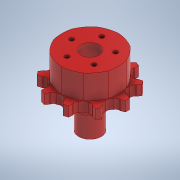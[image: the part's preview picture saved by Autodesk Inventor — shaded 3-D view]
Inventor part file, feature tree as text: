
AUTODESK INVENTOR PART (.ipt)
format: ipt  version: 2020 (Build 240168000, 168)  size: 395,264 bytes
history: native  units: mm
features: other x4, extrude x2, sketch x2
ambient origin geometry x8: Origin, YZ Plane, XZ Plane, XY Plane, X Axis, Y Axis, Z Axis, Center Point
bodies: Body1 (feature_tree)
feature tree (8):
  other  "Cilindric_rotate.ipt"
  extrude  "Выдавливание1"  Depth=10.0mm
  extrude  "Выдавливание2"  Depth=24.0mm
  other  "Твердое тело3::Cilindric_rotate.ipt"
  other  "Элемент создания тегов1"
  sketch  "Эскиз1"
  sketch  "Эскиз2"
  other  "Твердое тело1"
